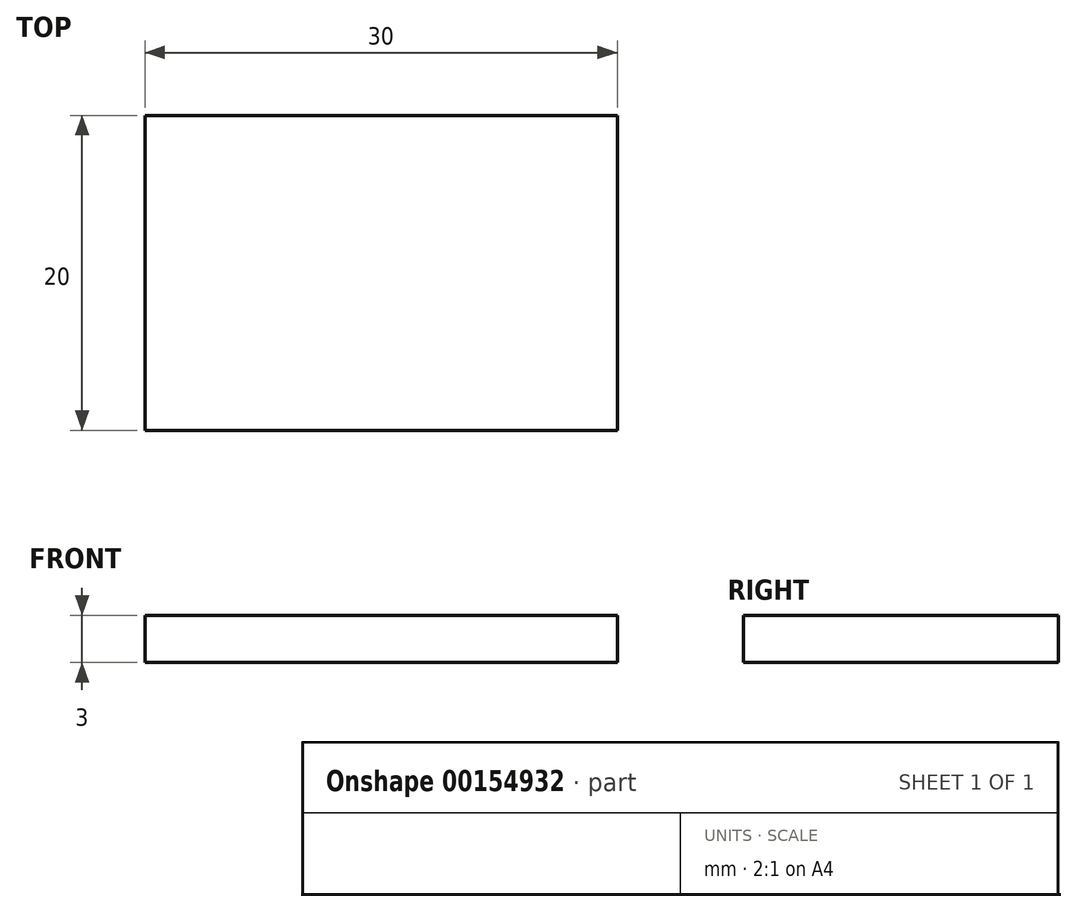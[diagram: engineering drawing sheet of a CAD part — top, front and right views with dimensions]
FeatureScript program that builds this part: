
annotation { "Feature Type Name" : "Feature", "Feature Type Description" : "" }
export const myFeature = defineFeature(function(context is Context, id is Id, definition is map)
    precondition{}
    {
        {
            var Q0;
            Q0=qCreatedBy(makeId("Top.planeOp"),FACE);
            var sketch = newSketch(context, id + "F0", { "sketchPlane" : qUnion([Q0])});
            skLineSegment(sketch, "E0.bottom", {"start": v(15, -10) * mm, "end": v(-15, -10) * mm});
            skLineSegment(sketch, "E0.top", {"start": v(15, 10) * mm, "end": v(-15, 10) * mm});
            skLineSegment(sketch, "E0.left", {"start": v(15, -10) * mm, "end": v(15, 10) * mm});
            skLineSegment(sketch, "E0.right", {"start": v(-15, -10) * mm, "end": v(-15, 10) * mm});
            skPoint(sketch, "E0.middle", {"position": v(0, 0) * mm});
            skSolve(sketch);
        }
        {
            var Q0;
            Q0=makeQuery(id+"F0.imprint","IMPRINT",FACE,{"disambiguationData":[TD([[makeQuery(id+"F0.imprint","IMPRINT",EDGE,{"derivedFrom":sQuery(id+"F0.wireOp",EDGE,"E0.bottom")}),-1.0]])]});
            extrude(context, id + "F1", {"entities" : qUnion([Q0]), "depth" : 3 * mm});
        }
    });
